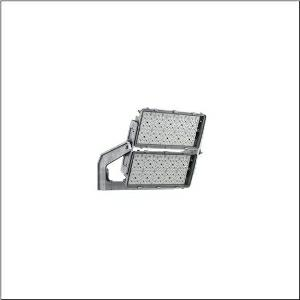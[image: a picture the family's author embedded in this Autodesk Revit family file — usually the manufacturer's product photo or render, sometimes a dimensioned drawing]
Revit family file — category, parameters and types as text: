
# Revit family: floodlight_fl_11_maxi_remote___rs07_5xa779514k01ba_6340
name_source: partatom
category: Lighting Fixtures
units: mm (PartAtom-declared; Revit-internal decimal feet)

## family parameters
Cut with Voids When Loaded = No
Host = Face
Light Source = No
Part Type = Normal
Room Calculation Point = No
Round Connector Dimension = Use Diameter
Shared = No

## types (1)
- --- (1 x LED, 75300 lm, 707.9 W, 5700K)
    Apparent Load = 708 VA
    CIE Flux Codes = 80 93 99 100 99
    Color Rendering = 90
    Color Temperature = 5700K
    Default Elevation = 1800 mm
    Description = Floodlight FL 11  maxi  Remote floodlight; light control with lens of PMMA; cover panel of toughened safety glass, transparent; light distribution: RS07, rotationally symmetric direct distribution, LEDcolour temperature: 5700K, rated luminous flux: 75.300lm, colour rendering: CRI > 90, light colour: 957; luminous efficacy: 106lm/W; brightness control: DMX+RDM; with terminal, 8-pole, max. 2.5mm², mains connection: 220..240V/380..400V AC, 50/60Hz, surge voltage resistance: line to ground: 10kV, ECG replaceable separately, LED unit replaceable without ESD environment, dustproof LED module, dimming range 10..100%; 708W floodlight with 2x LED unit of diecast aluminium, coated grey; length: 713mm / width: 651mm / height: 338mm; mounting bracket, of diecast aluminium, uncoated, natural, equipment: Longlife, protection rating (complete): IP66; insulation class (complete): insulation class I (protective earthing); certification: CE, ENEC, VDE; ball protection: ball impact resistance with accessories, impact resistance: IK07; only for outdoor installations, rated ambient temperature 10°C, permissible operating ambient temperature: -40..+40°C, permissible storage temperature: -40..+85°Cpackaging unit: 1 piece

Light Distribution: RS07
    Height = 320 mm
    Lamp = 1 x LED
    Lamp Light Flux = 75300 lm
    Lamp Power = 707.9 W
    Lamp count = 1
    Length = 712 mm
    Luminous efficacy = 106 lm/W
    Manufacturer = Siteco
    ModVariant = No
    Model = 5XA779514K01BA
    Mounting Place = Ceiling
    Mounting Type = Surface mounted
    Number of Poles = 1
    OnlyDefault = Yes
    Power Factor = 1
    Product Name = Floodlight FL 11 maxi Remote | RS07
    Product group = floodlight | ceiling mounted
    ProductGroupID = 301
    Protection Class = Protection class I
    Protection Degree = IP 66
    RLX_Detail_Level = 1
    RLX_Emergency_Light_Flux = 0 lm
    RLX_Emergency_Type = 0
    RLX_Emergency_Type_DB = No
    RlxData = <blob elided: 41169 chars, md5=10a8421c>
    Socket = socket
    Standby Power = 0 W
    System Light Flux = 75300 lm
    System Power = 708 W
    Type Comments = factory setting: luminous flux: 100 % | dim-lin: 254 | 740 mA
    Type Image = l_1349125.jpg
    URL = http://relux.com
    VarID = @adj_181408
    Voltage = 0 V
    Weight = 0.00 kg
    Width = 655 mm

## geometry (parser evidence)
native form markers: Blend x4, Sweep x13
no freeform markers — native parametric forms only
